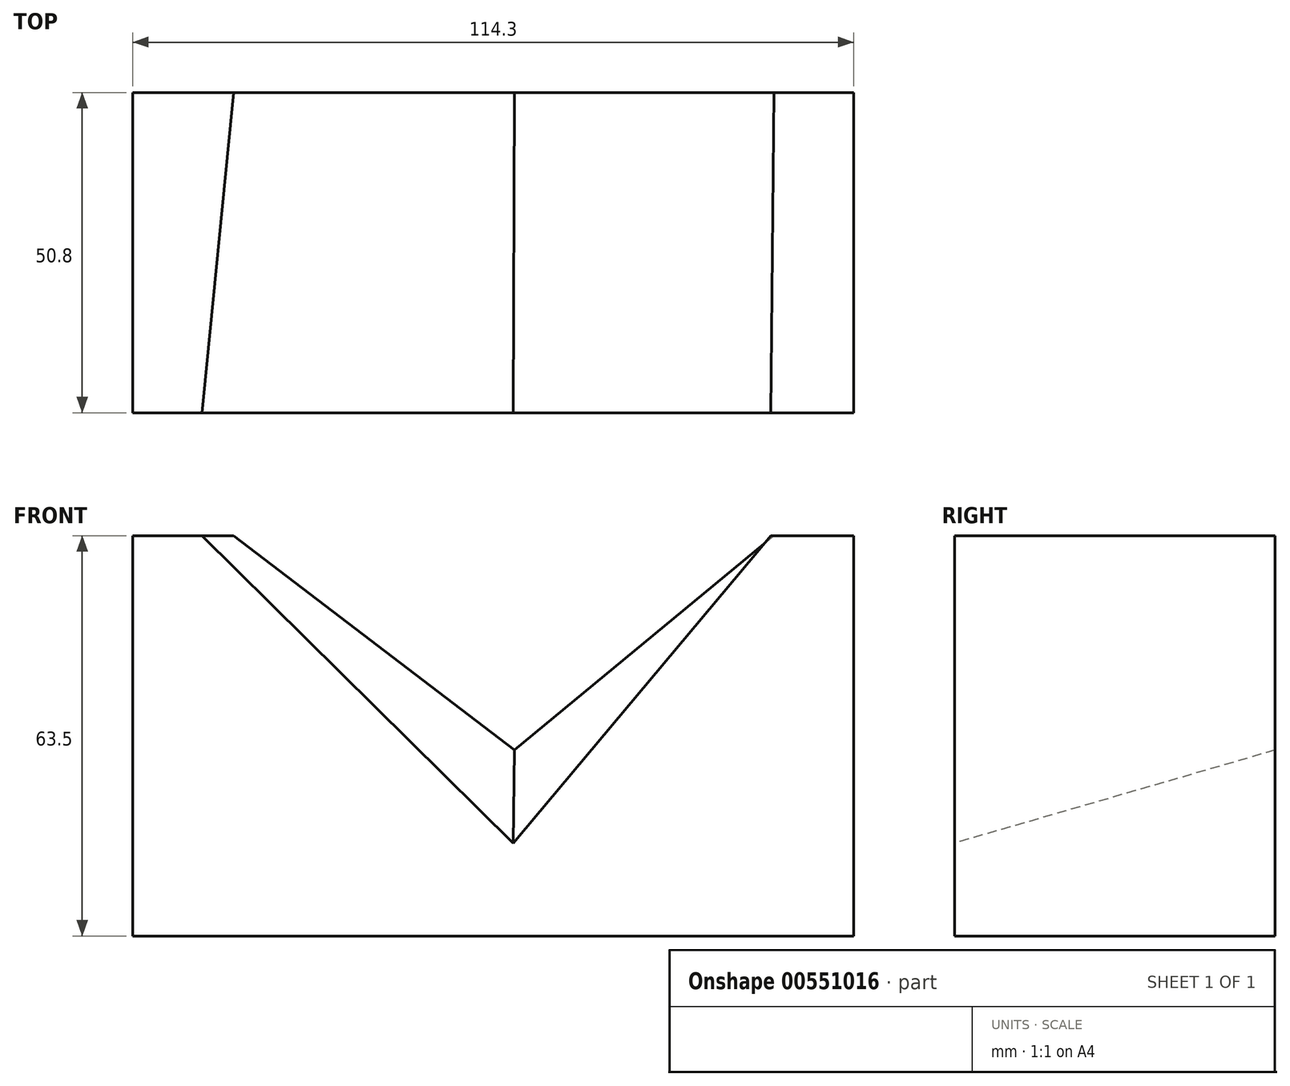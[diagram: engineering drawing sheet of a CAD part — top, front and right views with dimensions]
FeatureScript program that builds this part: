
annotation { "Feature Type Name" : "Feature", "Feature Type Description" : "" }
export const myFeature = defineFeature(function(context is Context, id is Id, definition is map)
    precondition{}
    {
        {
            var Q0;
            Q0=qCreatedBy(makeId("Front.planeOp"),FACE);
            var sketch = newSketch(context, id + "F0", { "sketchPlane" : qUnion([Q0])});
            skLineSegment(sketch, "E0", {"start": v(0, 0) * mm, "end": v(114.3, 0) * mm});
            skLineSegment(sketch, "E1", {"start": v(114.3, 0) * mm, "end": v(114.3, 63.5) * mm});
            skLineSegment(sketch, "E2", {"start": v(114.3, 63.5) * mm, "end": v(0, 63.5) * mm});
            skLineSegment(sketch, "E3", {"start": v(0, 63.5) * mm, "end": v(0, 0) * mm});
            skSolve(sketch);
        }
        {
            var Q0;
            Q0=makeQuery(id+"F0.imprint","IMPRINT",FACE,{"disambiguationData":[TD([[makeQuery(id+"F0.imprint","IMPRINT",EDGE,{"derivedFrom":sQuery(id+"F0.wireOp",EDGE,"E0")}),1.0]])]});
            extrude(context, id + "F1", {"entities" : qUnion([Q0]), "depth" : 50.8 * mm, "offsetDistance" : 25.4 * mm});
        }
        {
            var Q0;
            Q0=makeQuery(id+"F1.opExtrude","CAP_FACE",FACE,{"disambiguationData":[OSD([sQuery(id+"F0.wireOp",EDGE,"E0"),sQuery(id+"F0.wireOp",EDGE,"E1"),sQuery(id+"F0.wireOp",EDGE,"E2"),sQuery(id+"F0.wireOp",EDGE,"E3")])],"isStart":false});
            var sketch = newSketch(context, id + "F2", { "sketchPlane" : qUnion([Q0])});
            skLineSegment(sketch, "E4", {"start": v(10.95, 63.5) * mm, "end": v(60.35, 14.74) * mm});
            skLineSegment(sketch, "E5", {"start": v(60.35, 14.74) * mm, "end": v(101.17, 63.5) * mm});
            skLineSegment(sketch, "E6", {"start": v(101.17, 63.5) * mm, "end": v(10.95, 63.5) * mm});
            skSolve(sketch);
        }
        {
            var Q0;
            Q0=makeQuery(id+"F1.opExtrude","CAP_FACE",FACE,{"disambiguationData":[OSD([sQuery(id+"F0.wireOp",EDGE,"E0"),sQuery(id+"F0.wireOp",EDGE,"E1"),sQuery(id+"F0.wireOp",EDGE,"E2"),sQuery(id+"F0.wireOp",EDGE,"E3")])],"isStart":true});
            var sketch = newSketch(context, id + "F3", { "sketchPlane" : qUnion([Q0])});
            skLineSegment(sketch, "E7", {"start": v(-101.65, 63.5) * mm, "end": v(-60.51, 29.48) * mm});
            skLineSegment(sketch, "E8", {"start": v(-60.51, 29.48) * mm, "end": v(-15.97, 63.5) * mm});
            skLineSegment(sketch, "E9", {"start": v(-15.97, 63.5) * mm, "end": v(-101.65, 63.5) * mm});
            skSolve(sketch);
        }
        {
            var Q1;
            Q1=makeQuery(id+"F3.imprint","IMPRINT",FACE,{"disambiguationData":[TD([[makeQuery(id+"F3.imprint","IMPRINT",EDGE,{"derivedFrom":sQuery(id+"F3.wireOp",EDGE,"E7")}),1.0]])]});
            var Q2;
            Q2=makeQuery(id+"F2.imprint","IMPRINT",FACE,{"disambiguationData":[TD([[makeQuery(id+"F2.imprint","IMPRINT",EDGE,{"derivedFrom":sQuery(id+"F2.wireOp",EDGE,"E4")}),1.0]])]});
            loft(context, id + "F4", {"operationType" : NewBodyOperationType.REMOVE, "sheetProfilesArray" : [{ "sheetProfileEntities" : qUnion([Q1]) }, { "sheetProfileEntities" : qUnion([Q2]) }]});
        }
    });
